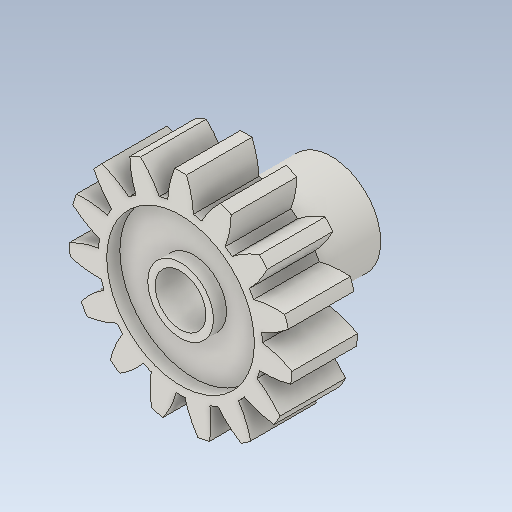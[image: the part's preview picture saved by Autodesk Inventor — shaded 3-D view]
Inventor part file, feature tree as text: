
AUTODESK INVENTOR PART (.ipt)
format: ipt  version: 2020.2 (Build 242310000, 310)  size: 214,528 bytes
history: imported  units: mm
features: imported_body x1
ambient origin geometry x8: Origin, YZ Plane, XZ Plane, XY Plane, X Axis, Y Axis, Z Axis, Center Point
bodies: Solide1 (imported_parasolid), Solid1 (imported_parasolid)
feature tree (1):
  imported_body  NMx_Import_Brep_tag  [imported B-rep: ~71 faces, bbox_mm=[13.581362, 13.506962, 9.2]]
